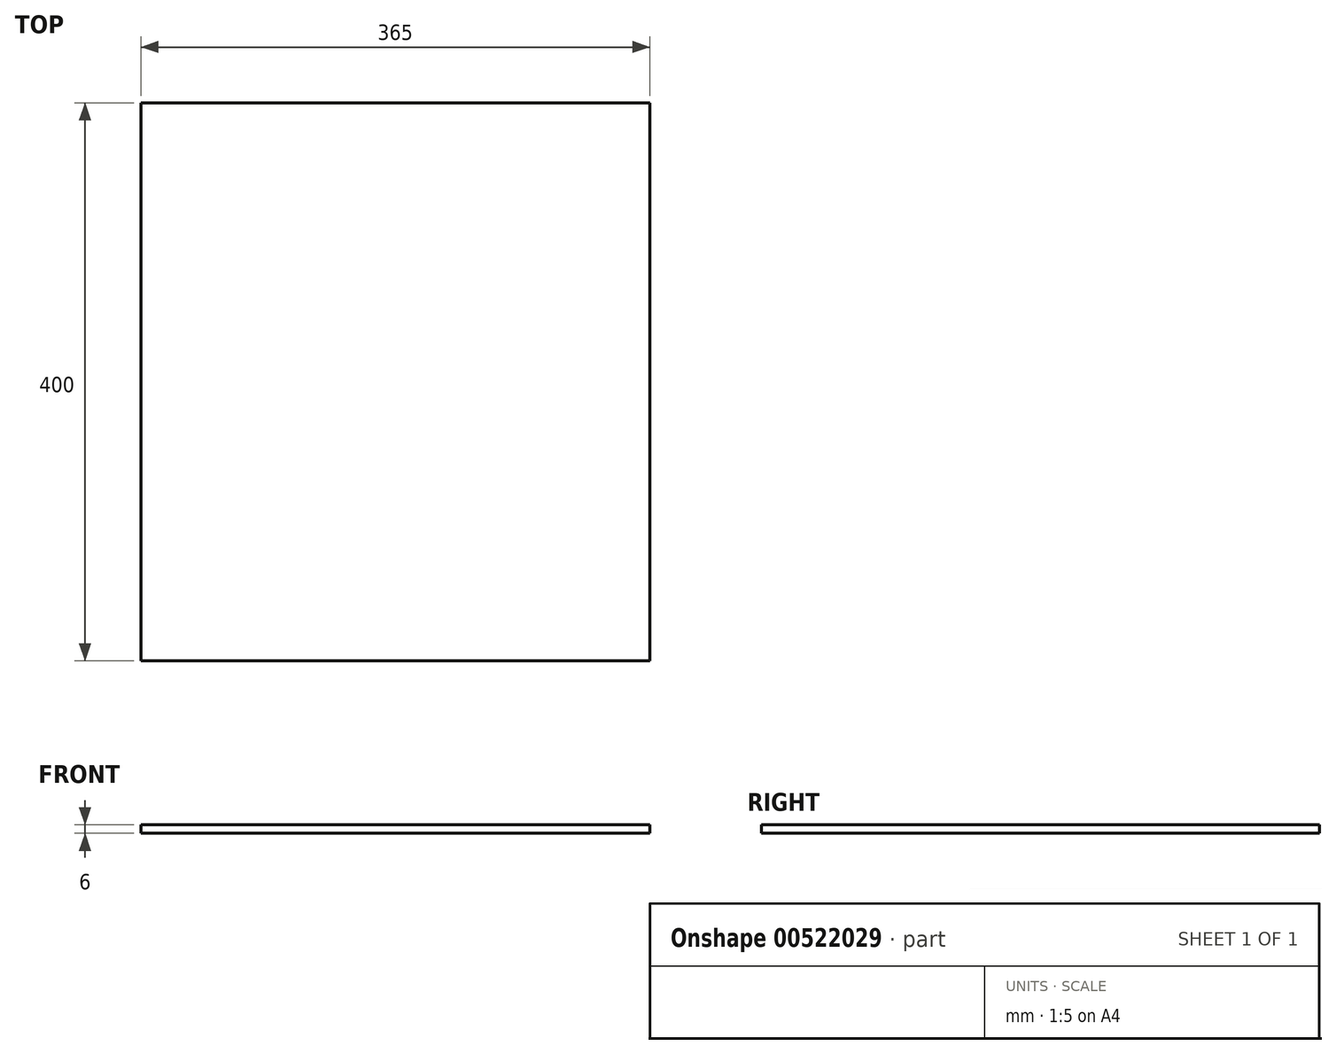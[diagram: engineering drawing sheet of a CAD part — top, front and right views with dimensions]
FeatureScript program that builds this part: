
annotation { "Feature Type Name" : "Feature", "Feature Type Description" : "" }
export const myFeature = defineFeature(function(context is Context, id is Id, definition is map)
    precondition{}
    {
        {
            var Q0;
            Q0=qCreatedBy(makeId("Top.planeOp"),FACE);
            var sketch = newSketch(context, id + "F0", { "sketchPlane" : qUnion([Q0])});
            skLineSegment(sketch, "E0.bottom", {"start": v(0, 0) * mm, "end": v(365, 0) * mm});
            skLineSegment(sketch, "E0.top", {"start": v(0, 400) * mm, "end": v(365, 400) * mm});
            skLineSegment(sketch, "E0.left", {"start": v(0, 0) * mm, "end": v(0, 400) * mm});
            skLineSegment(sketch, "E0.right", {"start": v(365, 0) * mm, "end": v(365, 400) * mm});
            skSolve(sketch);
        }
        {
            var Q0;
            Q0=makeQuery(id+"F0.imprint","IMPRINT",FACE,{"disambiguationData":[TD([[makeQuery(id+"F0.imprint","IMPRINT",EDGE,{"derivedFrom":sQuery(id+"F0.wireOp",EDGE,"E0.bottom")}),1.0]])]});
            extrude(context, id + "F1", {"entities" : qUnion([Q0]), "depth" : 6 * mm, "offsetDistance" : 25 * mm});
        }
    });
